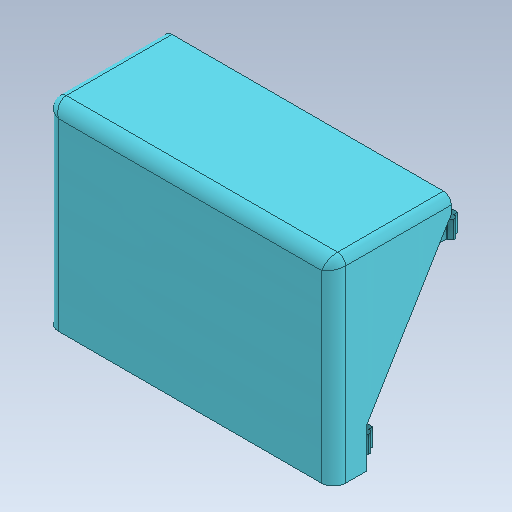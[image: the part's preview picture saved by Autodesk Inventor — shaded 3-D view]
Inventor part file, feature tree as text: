
AUTODESK INVENTOR PART (.ipt)
format: ipt  version: 2020 (Build 240168000, 168)  size: 448,512 bytes
history: native  units: in
note: dims shown in document units (in); Inventor stores cm internally (conversion verified against a paired STEP export)
features: reference x19, sketch x7, extrude x6, other x6, chamfer x4, plane x3, fillet x1, shell x1, helix x1, pattern_linear x1, mirror x1, projected_geometry x1
ambient origin geometry x8: Origin, YZ Plane, XZ Plane, XY Plane, X Axis, Y Axis, Z Axis, Center Point
bodies: Solid1 (feature_tree)
feature tree (51):
  sketch  "Sketch1"  dims[d0=1.0in d1=0.0in d2=0.1875in d3=0.0in d4=0.0in]
  plane  "Work Plane1"
  extrude  "Extrusion1"  Depth=0.1875in
  fillet  "Fillet1"  [1 undecoded]
  extrude  "Extrusion2"  Depth=0.25in TaperAngle=0.0deg
  shell  "Shell1"  Thickness=0.089in
  extrude  "Extrusion3"  Depth=0.0125in TaperAngle=45.0deg
  extrude  "Extrusion4"  Depth=0.0063in
  chamfer  "Chamfer1"  Distance=0.025in
  plane  "Work Plane2"
  helix  "Coil1"  [1 undecoded]
  pattern_linear  "Rectangular Pattern1"  Spacing1=0.025in  [1 undecoded]
  other  "Lip1"
  other  "Lip2"
  extrude  "Extrusion5"  Depth=0.175in
  chamfer  "Chamfer2"  Distance=0.025in
  extrude  "Extrusion6"  Depth=0.175in
  plane  "Work Plane3"
  mirror  "Mirror1"
  chamfer  "Chamfer3"  [1 undecoded]
  chamfer  "Chamfer4"  Distance=0.1in Angle=45.0deg
  reference  "Reference1"
  reference  "Reference4"
  reference  "Reference5"
  reference  "Reference6"
  sketch  "Sketch2"  dims[d5=0.125in d6=0.25in d7=0.0in d8=0.089in]
  reference  "Reference7"
  reference  "Reference8"
  sketch  "Sketch3"  dims[d9=0.25in d10=0.0in d11=0.0125in d12=0.125in d13=45.0deg]
  reference  "Reference9"
  reference  "Reference10"
  reference  "Reference11"
  sketch  "Sketch4"  dims[d14=0.0188in d15=0.0063in]
  reference  "Reference12"
  reference  "Reference13"
  sketch  "Sketch5"  dims[d16=60.0deg]
  projected_geometry  "Projected Loop1"
  sketch  "Sketch6"  dims[d17=0.2687in d18=0.025in d19=0.2687in]
  reference  "Reference14"
  reference  "Reference15"
  reference  "Reference16"
  reference  "Reference17"
  reference  "Reference18"
  reference  "Reference19"
  reference  "Reference20"
  reference  "Reference21"
  sketch  "Sketch7"  dims[d20=0.3937in d21=0.0in d22=90.0deg d23=90.0deg d24=0.0in d25=0.0in d27=0.7874in d29=4.125in d30=0.05in d31=0.0197in d32=0.0in d33=0.0in d34=0.0in d35=0.0in d36=0.05in d37=0.0197in d38=0.0in d39=0.0in d40=0.0in d41=0.0in d42=0.025in d43=0.175in d44=0.025in d45=0.175in d47=0.0in d48=0.1in d49=0.125in d50=45.0deg d51=0.065in d52=0.0in d53=0.045in d54=0.125in d55=45.0deg d56=0.1125in d57=0.1125in d58=0.1in d59=0.125in d60=45.0deg]
  other  "Readout.iam"
  other  "Base2:1"
  other  "Faceplate:1"
  other  "4x20 LCD:2"
note: 4 required parameter values undecoded (feature->parameter linkage not recoverable at this tier; creation-order binding heuristic only, values carry confidence <= 0.55)
